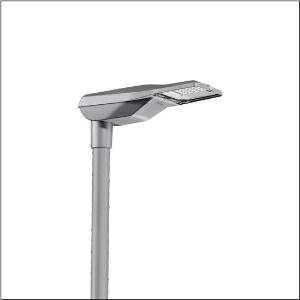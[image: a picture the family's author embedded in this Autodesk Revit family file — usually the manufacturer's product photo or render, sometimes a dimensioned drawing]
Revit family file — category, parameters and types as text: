
# Revit family: streetlight_sl_21_iq_micro___st0_8a_5xe1c61g08cb_671e
name_source: partatom
category: Lighting Fixtures
units: mm (PartAtom-declared; Revit-internal decimal feet)

## family parameters
Cut with Voids When Loaded = No
Host = Face
Light Source = No
Part Type = Normal
Room Calculation Point = No
Round Connector Dimension = Use Diameter
Shared = No

## types (1)
- --- (1 x LED, 2570 lm, 19.4 W, 2700K)
    Apparent Load = 19 VA
    CIE Flux Codes = 38 75 97 100 100
    Color Rendering = 70
    Color Temperature = 2700K
    Default Elevation = 1800 mm
    Description = Streetlight SL 21 iQ micro, mast luminaire, primary light control with lens, of PMMA, primary optical cover: cover, of toughened safety glass, transparent, light distribution: ST0.8a, light emission: direct distribution, primary light characteristic: asymmetric, installation type: post-top, side-entry, LED, High Power LED, rated luminous flux: 2.570lm, luminous efficacy: 133lm/W, light colour: 727, colour temperature: 2700K, control: Street-Remote, Auto-Match, Temp-Guard, Lumen-Switch, Night-Set, Smart-Wire, Light-Fading, Desk-Remote (wireless, voltage-free reading and setting of iQ features in the workshop via application-optimized NFC function/RFID function), optimised constant luminous flux control (CLO 2.0), pre-setting: linear dimming characteristic, mains connection: 220..240V, AC, 50/60Hz, start of lifetime: 19W, end of service life: 20W, reduction: 10W, luminaire housing, of diecast aluminium, powder-coated, Siteco® metallic grey (DB 702S), corrosivity category C5 mid according to DIN EN ISO 12944, please order mast flange separately, inclination adjustable: 0°, 5°, 10°, 15°, sealing non-destructively replaceable, multi-level sealing system, length: 528mm, width: 235mm, height: 110mm, mast flange for spigot size: 42mm (side-entry): 5XC10008XM4, 60/48mm (side-entry/post-top): 5XC10108XM2, 76/60mm (side-entry/post-top): 5XC10108XM1, protection rating (complete): IP66, insulation class (complete): insulation class II (safety insulation), certification: CE, ENEC, ENEC+, VDE, impact resistance: IK09, permissible operating ambient temperature for outdoor applications: -40..+50°C, standard-compliant lighting for roads and squares, packaging unit: 1 piece

Light Distribution: ST0.8a
    Height = 110 mm
    Lamp = 1 x LED
    Lamp Light Flux = 2570 lm
    Lamp Power = 19.4 W
    Lamp count = 1
    Length = 528 mm
    Luminous efficacy = 132 lm/W
    Manufacturer = Siteco
    ModVariant = No
    Model = 5XE1C61G08CB
    Number of Poles = 1
    OnlyDefault = Yes
    Power Factor = 1
    Product Name = Streetlight SL 21 iQ micro | ST0.8a
    Product group = mast luminaire | pylon top
    ProductGroupID = 6100
    Protection Class = Protection class II
    Protection Degree = IP 66
    RLX_Detail_Level = 1
    RLX_Emergency_Light_Flux = 0 lm
    RLX_Emergency_Type = 0
    RLX_Emergency_Type_DB = No
    RlxData = <blob elided: 100001 chars, md5=fe737444>
    Socket = socket
    Standby Power = 0 W
    System Light Flux = 2570 lm
    System Power = 19 W
    Type Comments = factory setting: luminous flux: 100 % | dim-lin: 254 | 387 mA
    Type Image = l_1006881.jpg
    URL = http://relux.com
    VarID = @adj_108087
    Voltage = 0 V
    Weight = 0.00 kg
    Width = 235 mm

## geometry (parser evidence)
native form markers: Blend x4, Sweep x12
no freeform markers — native parametric forms only
